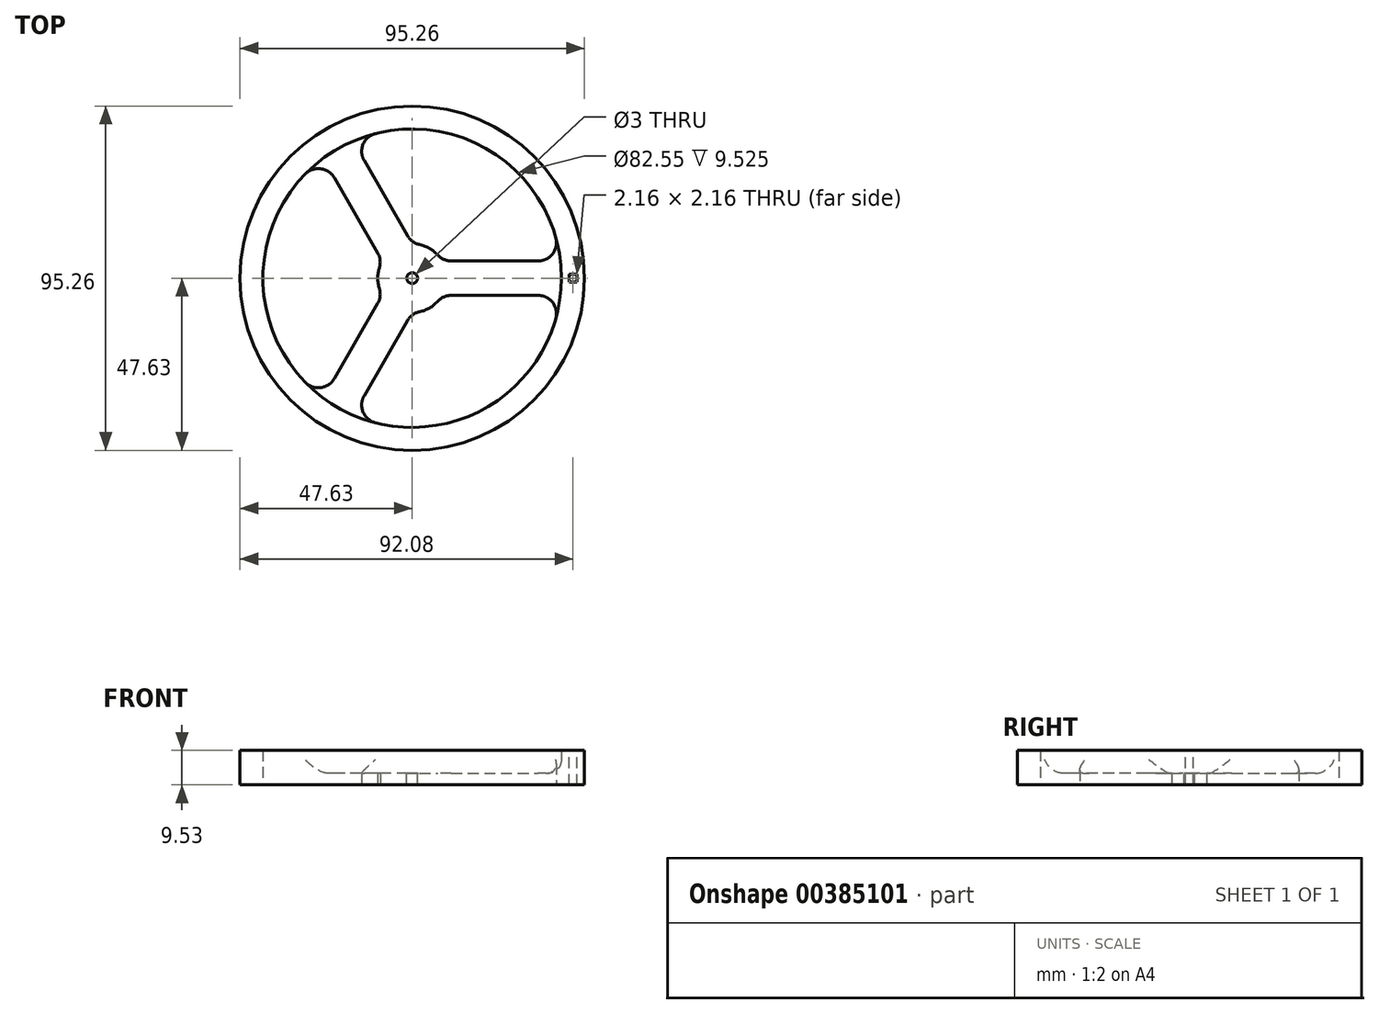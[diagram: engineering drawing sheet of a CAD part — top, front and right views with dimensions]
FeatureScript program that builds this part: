
annotation { "Feature Type Name" : "Feature", "Feature Type Description" : "" }
export const myFeature = defineFeature(function(context is Context, id is Id, definition is map)
    precondition{}
    {
        {
            var Q0;
            Q0=qCreatedBy(makeId("Top.planeOp"),FACE);
            var sketch = newSketch(context, id + "F0", { "sketchPlane" : qUnion([Q0])});
            skCircle(sketch, "E0", {"center": v(0, 0) * mm, "radius": 47.63 * mm});
            skArc(sketch, "E1", {"start": v(-24.62, 33.13) * mm, "mid": v(-41.28, 0) * mm, "end": v(-24.62, -33.13) * mm});
            skArc(sketch, "E2", {"start": v(-8.25, 4.76) * mm, "mid": v(-9.52, 0) * mm, "end": v(-8.25, -4.76) * mm});
            skLineSegment(sketch, "E3.0", {"start": v(8.25, -4.76) * mm, "end": v(41, -4.76) * mm});
            skLineSegment(sketch, "E4.0", {"start": v(8.25, 4.76) * mm, "end": v(41, 4.76) * mm});
            skLineSegment(sketch, "E5.1.0", {"start": v(0, 9.52) * mm, "end": v(-16.38, 37.89) * mm});
            skLineSegment(sketch, "E5.1.1", {"start": v(-8.25, 4.76) * mm, "end": v(-24.62, 33.13) * mm});
            skLineSegment(sketch, "E5.2.0", {"start": v(-8.25, -4.76) * mm, "end": v(-24.62, -33.13) * mm});
            skLineSegment(sketch, "E5.2.1", {"start": v(0, -9.53) * mm, "end": v(-16.38, -37.89) * mm});
            skArc(sketch, "E6.trimOffspring", {"start": v(-16.38, -37.89) * mm, "mid": v(20.64, -35.75) * mm, "end": v(41, -4.76) * mm});
            skArc(sketch, "E7.trimOffspring", {"start": v(41, 4.76) * mm, "mid": v(20.64, 35.75) * mm, "end": v(-16.38, 37.89) * mm});
            skArc(sketch, "E8.trimOffspring", {"start": v(8.25, 4.76) * mm, "mid": v(4.76, 8.25) * mm, "end": v(0, 9.53) * mm});
            skArc(sketch, "E9.trimOffspring", {"start": v(0, -9.53) * mm, "mid": v(4.76, -8.25) * mm, "end": v(8.25, -4.76) * mm});
            skSolve(sketch);
        }
        {
            var Q0;
            Q0=makeQuery(id+"F0.imprint","IMPRINT",FACE,{"disambiguationData":[TD([[makeQuery(id+"F0.imprint","IMPRINT",EDGE,{"derivedFrom":sQuery(id+"F0.wireOp",EDGE,"E0")}),1.0]])]});
            var Q1;
            Q1=makeQuery(id+"F0.imprint","IMPRINT",FACE,{"disambiguationData":[TD([[makeQuery(id+"F0.imprint","IMPRINT",EDGE,{"derivedFrom":sQuery(id+"F0.wireOp",EDGE,"E2")}),1.0]])]});
            extrude(context, id + "F1", {"entities" : qUnion([Q0, Q1]), "depth" : 9.52 * mm});
        }
        {
            var Q0;
            Q0=makeQuery(id+"F1.opExtrude","CAP_FACE",FACE,{"disambiguationData":[OSD([sQuery(id+"F0.wireOp",EDGE,"E0"),sQuery(id+"F0.wireOp",EDGE,"E1"),sQuery(id+"F0.wireOp",EDGE,"E2"),sQuery(id+"F0.wireOp",EDGE,"E3.0"),sQuery(id+"F0.wireOp",EDGE,"E4.0"),sQuery(id+"F0.wireOp",EDGE,"E5.1.0"),sQuery(id+"F0.wireOp",EDGE,"E5.1.1"),sQuery(id+"F0.wireOp",EDGE,"E5.2.0"),sQuery(id+"F0.wireOp",EDGE,"E5.2.1"),sQuery(id+"F0.wireOp",EDGE,"E6.trimOffspring"),sQuery(id+"F0.wireOp",EDGE,"E7.trimOffspring"),sQuery(id+"F0.wireOp",EDGE,"E8.trimOffspring"),sQuery(id+"F0.wireOp",EDGE,"E9.trimOffspring")])],"isStart":false});
            var sketch = newSketch(context, id + "F2", { "sketchPlane" : qUnion([Q0])});
            skCircle(sketch, "E10", {"center": v(0, 0) * mm, "radius": 41.28 * mm});
            skCircle(sketch, "E11", {"center": v(0, 0) * mm, "radius": 1.5 * mm});
            skSolve(sketch);
        }
        {
            var Q0;
            Q0=makeQuery(id+"F2.imprint","IMPRINT",FACE,{"disambiguationData":[TD([[makeQuery(id+"F2.imprint","IMPRINT",EDGE,{"derivedFrom":sQuery(id+"F2.wireOp",EDGE,"E11")}),1.0]])]});
            extrude(context, id + "F3", {"entities" : qUnion([Q0]), "operationType" : NewBodyOperationType.REMOVE, "endBound" : BoundingType.THROUGH_ALL, "oppositeDirection" : true, "depth" : 25.4 * mm});
        }
        {
            var Q0;
            Q0=makeQuery(id+"F2.imprint","IMPRINT",FACE,{"disambiguationData":[TD([[makeQuery(id+"F2.imprint","IMPRINT",EDGE,{"derivedFrom":sQuery(id+"F2.wireOp",EDGE,"E11")}),-1.0]])]});
            var Q1;
            Q1=sQuery(id+"F2.wireOp",EDGE,"E10");
            extrude(context, id + "F4", {"entities" : qUnion([Q0]), "operationType" : NewBodyOperationType.REMOVE, "surfaceEntities" : qUnion([Q1]), "oppositeDirection" : true, "depth" : 6.35 * mm});
        }
        {
            var Q0;
            {var subQ0=sQuery(id+"F2.wireOp",EDGE,"E10");Q0=makeQuery(id+"F4.boolean.opBoolean","COPY",EDGE,{"derivedFrom":makeQuery(id+"F4.opExtrude","CAP_EDGE",EDGE,{"disambiguationData":[OSD([subQ0]),TDD([makeQuery(id+"F2.imprint","IMPRINT",EDGE,{"disambiguationData":[TD([[makeQuery(id+"F2.imprint","INTERSECT",VERTEX,{"derivedFrom":[makeQuery(id+"F1.opExtrude","CAP_EDGE",EDGE,{"disambiguationData":[OSD([sQuery(id+"F0.wireOp",EDGE,"E5.1.1")])],"isStart":false}),subQ0]}),1.0]])],"derivedFrom":subQ0})])],"isStart":false})});}
            var Q1;
            {var subQ0=sQuery(id+"F2.wireOp",EDGE,"E10");Q1=makeQuery(id+"F4.boolean.opBoolean","COPY",EDGE,{"derivedFrom":makeQuery(id+"F4.opExtrude","CAP_EDGE",EDGE,{"disambiguationData":[OSD([subQ0]),TDD([makeQuery(id+"F2.imprint","IMPRINT",EDGE,{"disambiguationData":[TD([[makeQuery(id+"F2.imprint","INTERSECT",VERTEX,{"derivedFrom":[makeQuery(id+"F1.opExtrude","CAP_EDGE",EDGE,{"disambiguationData":[OSD([sQuery(id+"F0.wireOp",EDGE,"E5.2.0")])],"isStart":false}),subQ0]}),-1.0]])],"derivedFrom":subQ0})])],"isStart":false})});}
            var Q2;
            {var subQ0=sQuery(id+"F2.wireOp",EDGE,"E10");Q2=makeQuery(id+"F4.boolean.opBoolean","COPY",EDGE,{"derivedFrom":makeQuery(id+"F4.opExtrude","CAP_EDGE",EDGE,{"disambiguationData":[OSD([subQ0]),TDD([makeQuery(id+"F2.imprint","IMPRINT",EDGE,{"disambiguationData":[TD([[makeQuery(id+"F2.imprint","INTERSECT",VERTEX,{"derivedFrom":[makeQuery(id+"F1.opExtrude","CAP_EDGE",EDGE,{"disambiguationData":[OSD([sQuery(id+"F0.wireOp",EDGE,"E3.0")])],"isStart":false}),subQ0]}),-1.0]])],"derivedFrom":subQ0})])],"isStart":false})});}
            fillet(context, id + "F5", {"entities" : qUnion([Q0, Q1, Q2]), "radius" : 3.8 * mm, "allowEdgeOverflow" : false});
        }
        {
            var Q0;
            Q0=makeQuery(id+"F1.opExtrude","SWEPT_EDGE",EDGE,{"disambiguationData":[OSD([sQuery(id+"F0.wireOp",EDGE,"E1"),sQuery(id+"F0.wireOp",EDGE,"E5.1.1")])]});
            var Q1;
            Q1=makeQuery(id+"F1.opExtrude","SWEPT_EDGE",EDGE,{"disambiguationData":[OSD([sQuery(id+"F0.wireOp",EDGE,"E5.1.0"),sQuery(id+"F0.wireOp",EDGE,"E7.trimOffspring")])]});
            var Q2;
            Q2=makeQuery(id+"F1.opExtrude","SWEPT_EDGE",EDGE,{"disambiguationData":[OSD([sQuery(id+"F0.wireOp",EDGE,"E4.0"),sQuery(id+"F0.wireOp",EDGE,"E7.trimOffspring")])]});
            var Q3;
            Q3=makeQuery(id+"F1.opExtrude","SWEPT_EDGE",EDGE,{"disambiguationData":[OSD([sQuery(id+"F0.wireOp",EDGE,"E3.0"),sQuery(id+"F0.wireOp",EDGE,"E6.trimOffspring")])]});
            var Q4;
            Q4=makeQuery(id+"F1.opExtrude","SWEPT_EDGE",EDGE,{"disambiguationData":[OSD([sQuery(id+"F0.wireOp",EDGE,"E4.0"),sQuery(id+"F0.wireOp",EDGE,"E8.trimOffspring")])]});
            var Q5;
            Q5=makeQuery(id+"F1.opExtrude","SWEPT_EDGE",EDGE,{"disambiguationData":[OSD([sQuery(id+"F0.wireOp",EDGE,"E5.1.0"),sQuery(id+"F0.wireOp",EDGE,"E8.trimOffspring")])]});
            var Q6;
            Q6=makeQuery(id+"F1.opExtrude","SWEPT_EDGE",EDGE,{"disambiguationData":[OSD([sQuery(id+"F0.wireOp",EDGE,"E2"),sQuery(id+"F0.wireOp",EDGE,"E5.1.1")])]});
            var Q7;
            Q7=makeQuery(id+"F1.opExtrude","SWEPT_EDGE",EDGE,{"disambiguationData":[OSD([sQuery(id+"F0.wireOp",EDGE,"E2"),sQuery(id+"F0.wireOp",EDGE,"E5.2.0")])]});
            var Q8;
            Q8=makeQuery(id+"F1.opExtrude","SWEPT_EDGE",EDGE,{"disambiguationData":[OSD([sQuery(id+"F0.wireOp",EDGE,"E3.0"),sQuery(id+"F0.wireOp",EDGE,"E9.trimOffspring")])]});
            var Q9;
            Q9=makeQuery(id+"F1.opExtrude","SWEPT_EDGE",EDGE,{"disambiguationData":[OSD([sQuery(id+"F0.wireOp",EDGE,"E5.2.1"),sQuery(id+"F0.wireOp",EDGE,"E9.trimOffspring")])]});
            var Q10;
            Q10=makeQuery(id+"F1.opExtrude","SWEPT_EDGE",EDGE,{"disambiguationData":[OSD([sQuery(id+"F0.wireOp",EDGE,"E1"),sQuery(id+"F0.wireOp",EDGE,"E5.2.0")])]});
            var Q11;
            Q11=makeQuery(id+"F1.opExtrude","SWEPT_EDGE",EDGE,{"disambiguationData":[OSD([sQuery(id+"F0.wireOp",EDGE,"E5.2.1"),sQuery(id+"F0.wireOp",EDGE,"E6.trimOffspring")])]});
            fillet(context, id + "F6", {"entities" : qUnion([Q0, Q1, Q2, Q3, Q4, Q5, Q6, Q7, Q8, Q9, Q10, Q11]), "radius" : 5.08 * mm, "tangentPropagation" : true, "allowEdgeOverflow" : false});
        }
        {
            var Q0;
            Q0=makeQuery(id+"F2.imprint","IMPRINT",FACE,{"disambiguationData":[TD([[makeQuery(id+"F2.imprint","IMPRINT",EDGE,{"derivedFrom":makeQuery(id+"F1.opExtrude","CAP_EDGE",EDGE,{"disambiguationData":[OSD([sQuery(id+"F0.wireOp",EDGE,"E0")])],"isStart":false})}),1.0]])]});
            var sketch = newSketch(context, id + "F7", { "sketchPlane" : qUnion([Q0])});
            skLineSegment(sketch, "E12.bottom", {"start": v(45.53, 1.08) * mm, "end": v(43.37, 1.08) * mm});
            skLineSegment(sketch, "E12.top", {"start": v(45.53, -1.08) * mm, "end": v(43.37, -1.08) * mm});
            skLineSegment(sketch, "E12.left", {"start": v(45.53, 1.08) * mm, "end": v(45.53, -1.08) * mm});
            skLineSegment(sketch, "E12.right", {"start": v(43.37, 1.08) * mm, "end": v(43.37, -1.08) * mm});
            skPoint(sketch, "E12.middle", {"position": v(44.45, 0) * mm});
            skSolve(sketch);
        }
        {
            var Q0;
            Q0=makeQuery(id+"F7.imprint","IMPRINT",FACE,{"disambiguationData":[TD([[makeQuery(id+"F7.imprint","IMPRINT",EDGE,{"derivedFrom":sQuery(id+"F7.wireOp",EDGE,"E12.bottom")}),1.0]])]});
            extrude(context, id + "F8", {"entities" : qUnion([Q0]), "operationType" : NewBodyOperationType.REMOVE, "endBound" : BoundingType.THROUGH_ALL, "oppositeDirection" : true, "depth" : 25.4 * mm});
        }
    });
